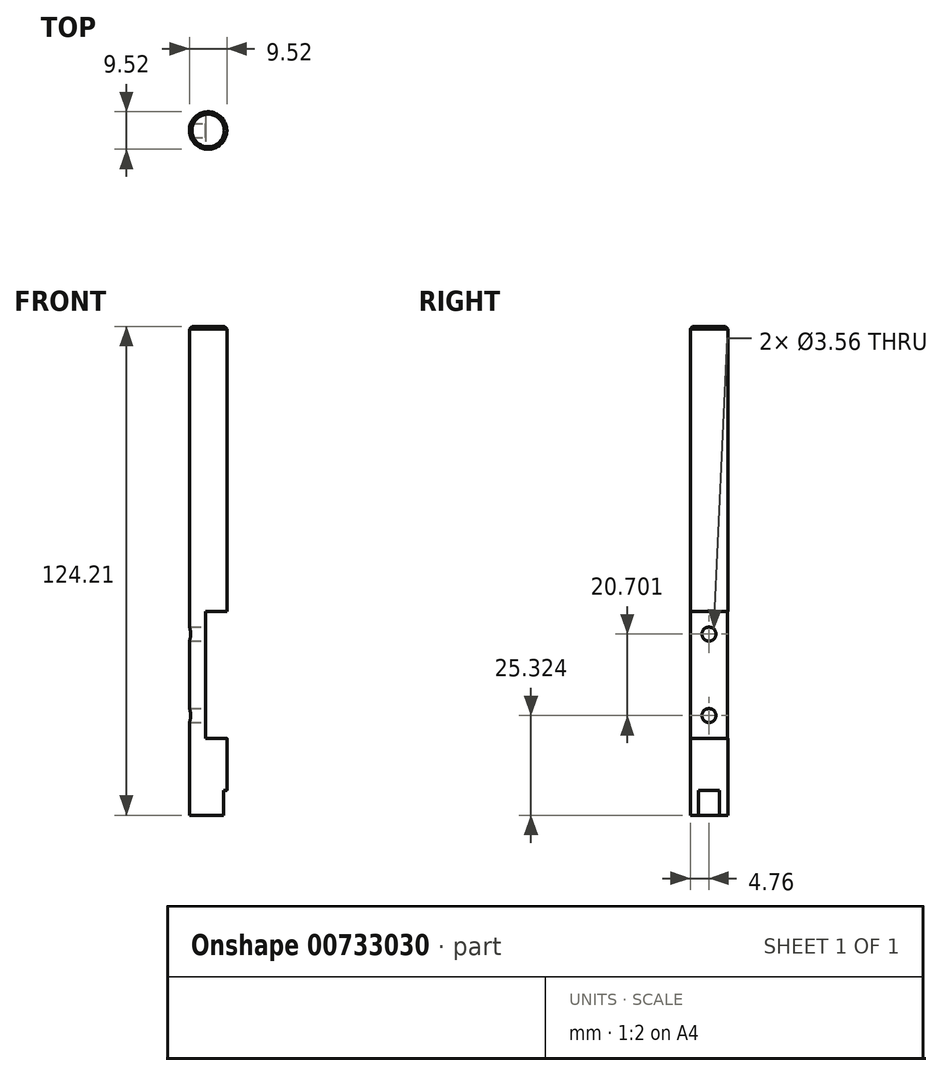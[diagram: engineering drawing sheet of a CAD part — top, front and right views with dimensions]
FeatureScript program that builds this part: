
annotation { "Feature Type Name" : "Feature", "Feature Type Description" : "" }
export const myFeature = defineFeature(function(context is Context, id is Id, definition is map)
    precondition{}
    {
        {
            var Q0;
            Q0=qCreatedBy(makeId("Top.planeOp"),FACE);
            var sketch = newSketch(context, id + "F0", { "sketchPlane" : qUnion([Q0])});
            skCircle(sketch, "E0", {"center": v(0, 0) * mm, "radius": 4.76 * mm});
            skSolve(sketch);
        }
        {
            var Q0;
            Q0=makeQuery(id+"F0.imprint","IMPRINT",FACE,{"disambiguationData":[TD([[makeQuery(id+"F0.imprint","IMPRINT",EDGE,{"derivedFrom":sQuery(id+"F0.wireOp",EDGE,"E0")}),1.0]])]});
            extrude(context, id + "F1", {"entities" : qUnion([Q0]), "depth" : 117.86 * mm, "offsetDistance" : 25.4 * mm});
        }
        {
            var Q0;
            Q0=qCreatedBy(makeId("Right.planeOp"),FACE);
            var sketch = newSketch(context, id + "F2", { "sketchPlane" : qUnion([Q0])});
            skLineSegment(sketch, "E1.bottom", {"start": v(4.76, 45.47) * mm, "end": v(-4.76, 45.47) * mm});
            skLineSegment(sketch, "E1.top", {"start": v(4.76, 13.2) * mm, "end": v(-4.76, 13.2) * mm});
            skLineSegment(sketch, "E1.left", {"start": v(4.76, 45.47) * mm, "end": v(4.76, 13.2) * mm});
            skLineSegment(sketch, "E1.right", {"start": v(-4.76, 45.47) * mm, "end": v(-4.76, 13.2) * mm});
            skSolve(sketch);
        }
        {
            var Q0;
            Q0 = qSketchRegion(id + "F2", true);
            extrude(context, id + "F3", {"entities" : qUnion([Q0]), "operationType" : NewBodyOperationType.REMOVE, "depth" : 25.4 * mm, "offsetDistance" : 25.4 * mm});
        }
        {
            var Q0;
            Q0 = qSketchRegion(id + "F2", true);
            extrude(context, id + "F4", {"entities" : qUnion([Q0]), "operationType" : NewBodyOperationType.REMOVE, "oppositeDirection" : true, "depth" : 0.7 * mm, "offsetDistance" : 25.4 * mm});
        }
        {
            var Q0;
            Q0=makeQuery(id+"F2.imprint","IMPRINT",FACE,{"disambiguationData":[TD([[makeQuery(id+"F2.imprint","IMPRINT",EDGE,{"derivedFrom":sQuery(id+"F2.wireOp",EDGE,"E1.bottom")}),1.0]])]});
            var sketch = newSketch(context, id + "F5", { "sketchPlane" : qUnion([Q0])});
            skCircle(sketch, "E2", {"center": v(0, 39.67) * mm, "radius": 1.78 * mm});
            skCircle(sketch, "E3", {"center": v(0, 18.97) * mm, "radius": 1.78 * mm});
            skSolve(sketch);
        }
        {
            var Q0;
            Q0 = qSketchRegion(id + "F5", true);
            extrude(context, id + "F6", {"entities" : qUnion([Q0]), "operationType" : NewBodyOperationType.REMOVE, "oppositeDirection" : true, "depth" : 25.4 * mm, "offsetDistance" : 25.4 * mm});
        }
        {
            var Q0;
            Q0=makeQuery(id+"F0.imprint","IMPRINT",FACE,{"disambiguationData":[TD([[makeQuery(id+"F0.imprint","IMPRINT",EDGE,{"derivedFrom":sQuery(id+"F0.wireOp",EDGE,"E0")}),1.0]])]});
            var sketch = newSketch(context, id + "F7", { "sketchPlane" : qUnion([Q0])});
            skArc(sketch, "E4", {"start": v(3.93, 2.7) * mm, "mid": v(-4.76, 0) * mm, "end": v(3.93, -2.7) * mm});
            skLineSegment(sketch, "E5", {"start": v(3.93, -2.7) * mm, "end": v(3.93, 2.7) * mm});
            skSolve(sketch);
        }
        {
            var Q0;
            Q0 = qSketchRegion(id + "F7", true);
            extrude(context, id + "F8", {"entities" : qUnion([Q0]), "operationType" : NewBodyOperationType.ADD, "oppositeDirection" : true, "depth" : 6.35 * mm, "offsetDistance" : 25.4 * mm});
        }
        {
            var Q0;
            Q0=makeQuery(id+"F1.opExtrude","CAP_EDGE",EDGE,{"disambiguationData":[OSD([sQuery(id+"F0.wireOp",EDGE,"E0")])],"isStart":false});
            chamfer(context, id + "F9", {"entities" : qUnion([Q0]), "width" : 0.64 * mm, "tangentPropagation" : true});
        }
    });
